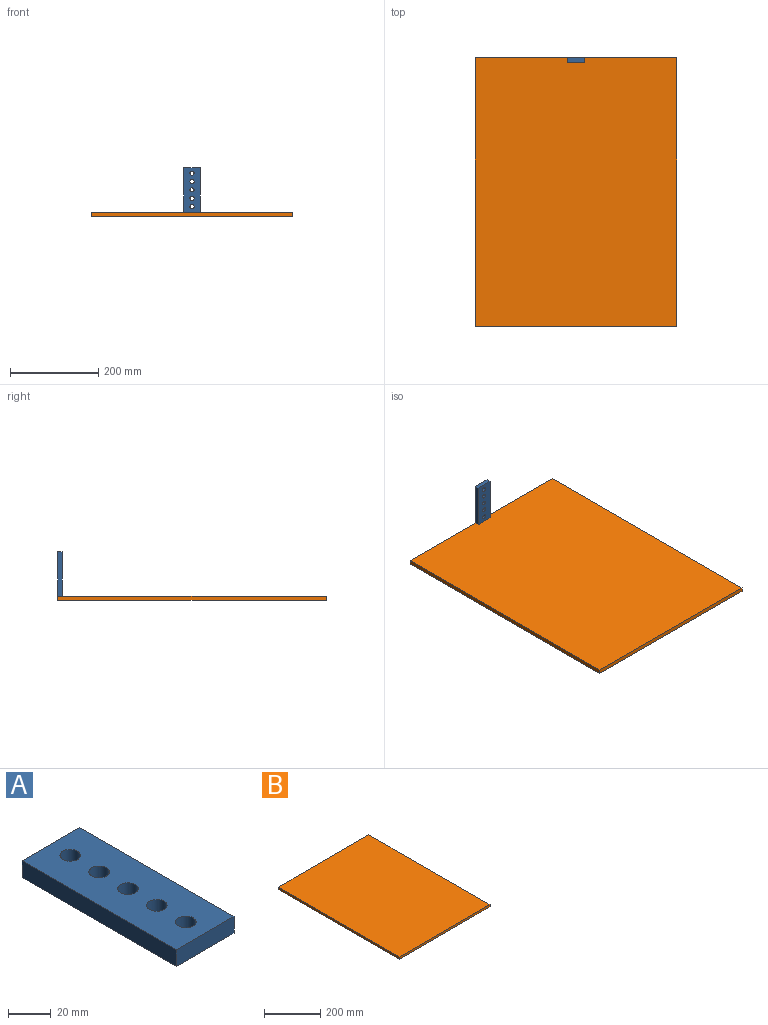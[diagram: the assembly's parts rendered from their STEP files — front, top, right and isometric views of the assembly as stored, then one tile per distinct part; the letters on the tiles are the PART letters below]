
ASSEMBLY  parts=2 mates=1
PART A: 11 faces, bbox 38.1x101.6x9.5 mm
  f0: plane 38.1x9.53mm, normal (0,1,0), area 362.9mm2, adj f1,f8,f9,f10
  f1: plane 101.6x9.53mm, normal (-1,0,0), area 967.7mm2, adj f0,f2,f9,f10
  f2: plane 38.1x9.53mm, normal (0,-1,0), area 362.9mm2, adj f1,f8,f9,f10
  f3: cylinder r=4.76mm len=9.53mm, axis (0,0,-1), area 285mm2, adj f9,f10
  f4: cylinder r=4.76mm len=9.53mm, axis (0,0,-1), area 285mm2, adj f9,f10
  f5: cylinder r=4.76mm len=9.53mm, axis (0,0,-1), area 285mm2, adj f9,f10
  f6: cylinder r=4.76mm len=9.53mm, axis (0,0,-1), area 285mm2, adj f9,f10
  f7: cylinder r=4.76mm len=9.53mm, axis (0,0,-1), area 285mm2, adj f9,f10
  f8: plane 101.6x9.53mm, normal (1,0,0), area 967.7mm2, adj f0,f2,f9,f10
  f9: plane 101.6x38.1mm, normal (0,0,1), area 3514.7mm2, adj f0,f1,f2,f3,f4,f5,f6,f7
  f10: plane 101.6x38.1mm, normal (0,0,-1), area 3514.7mm2, adj f0,f1,f2,f3,f4,f5,f6,f7
PART B: 6 faces, bbox 457.2x609.6x9.5 mm
  f0: plane 457.2x9.53mm, normal (0,1,0), area 4354.8mm2, adj f1,f3,f4,f5
  f1: plane 609.6x9.53mm, normal (-1,0,0), area 5806.4mm2, adj f0,f2,f4,f5
  f2: plane 457.2x9.53mm, normal (0,-1,0), area 4354.8mm2, adj f1,f3,f4,f5
  f3: plane 609.6x9.53mm, normal (1,0,0), area 5806.4mm2, adj f0,f2,f4,f5
  f4: plane 609.6x457.2mm, normal (0,0,1), area 278709.1mm2, adj f0,f1,f2,f3
  f5: plane 609.6x457.2mm, normal (0,0,-1), area 278709.1mm2, adj f0,f1,f2,f3
PLACE A rot(axis=(-1,0,0),90deg) t=(-90.75,337.29,199.88)mm
PLACE B t=(92.6,-213.16,135.4)mm fixed
MATE fastened A.f0 <-> B.f4  axis (0,0,-1) through (-89.07,346.82,144.93)mm
